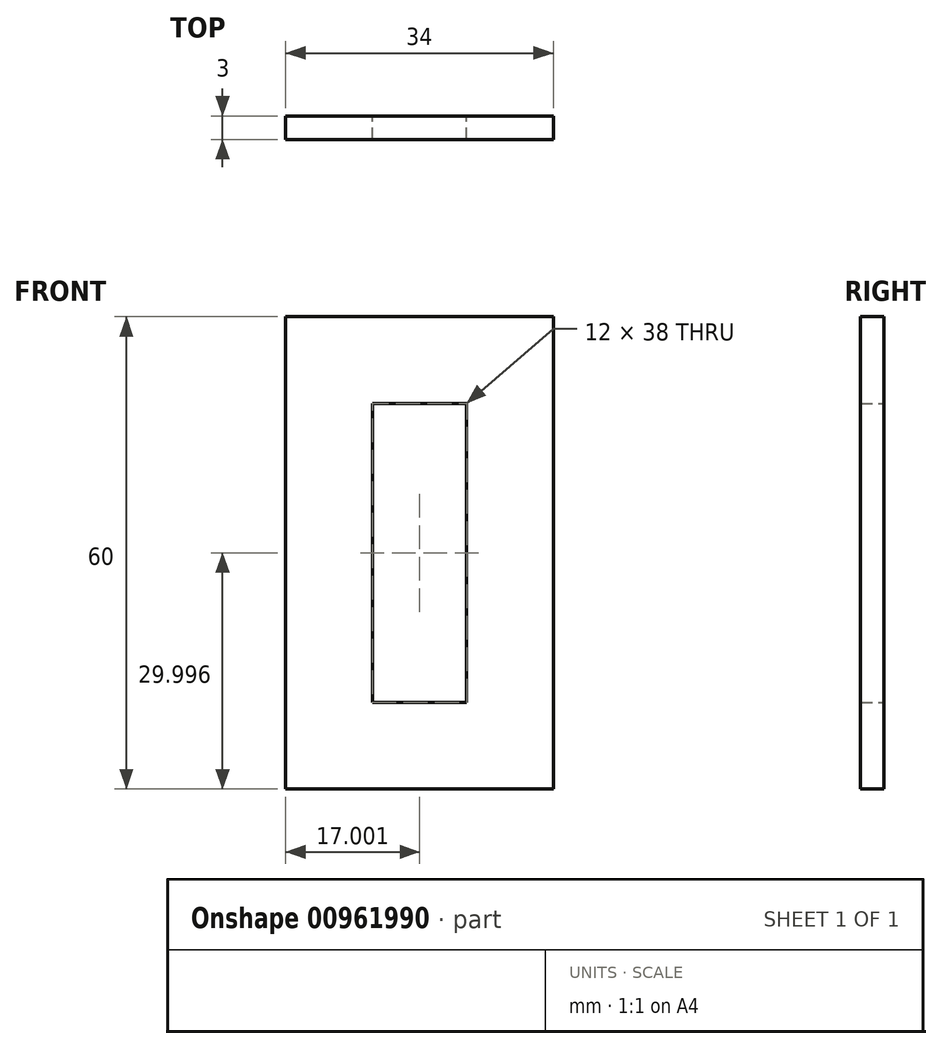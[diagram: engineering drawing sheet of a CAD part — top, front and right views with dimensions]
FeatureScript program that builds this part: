
annotation { "Feature Type Name" : "Feature", "Feature Type Description" : "" }
export const myFeature = defineFeature(function(context is Context, id is Id, definition is map)
    precondition{}
    {
        {
            var Q0;
            Q0=qCreatedBy(makeId("Front.planeOp"),FACE);
            var sketch = newSketch(context, id + "F0", { "sketchPlane" : qUnion([Q0])});
            skLineSegment(sketch, "E0.bottom", {"start": v(-5.63, 36.04) * mm, "end": v(28.37, 36.04) * mm});
            skLineSegment(sketch, "E0.top", {"start": v(-5.63, -23.96) * mm, "end": v(28.37, -23.96) * mm});
            skLineSegment(sketch, "E0.left", {"start": v(-5.63, 36.04) * mm, "end": v(-5.63, -23.96) * mm});
            skLineSegment(sketch, "E0.right", {"start": v(28.37, 36.04) * mm, "end": v(28.37, -23.96) * mm});
            skLineSegment(sketch, "E1.0", {"start": v(5.37, 25.04) * mm, "end": v(17.37, 25.04) * mm});
            skLineSegment(sketch, "E1.1", {"start": v(5.37, 25.04) * mm, "end": v(5.37, -12.96) * mm});
            skLineSegment(sketch, "E1.2", {"start": v(5.37, -12.96) * mm, "end": v(17.37, -12.96) * mm});
            skLineSegment(sketch, "E1.3", {"start": v(17.37, 25.04) * mm, "end": v(17.37, -12.96) * mm});
            skSolve(sketch);
        }
        {
            var Q0;
            Q0=makeQuery(id+"F0.imprint","IMPRINT",FACE,{"disambiguationData":[TD([[makeQuery(id+"F0.imprint","IMPRINT",EDGE,{"derivedFrom":sQuery(id+"F0.wireOp",EDGE,"E0.bottom")}),-1.0]])]});
            extrude(context, id + "F1", {"entities" : qUnion([Q0]), "depth" : 3 * mm, "offsetDistance" : 25 * mm});
        }
    });
